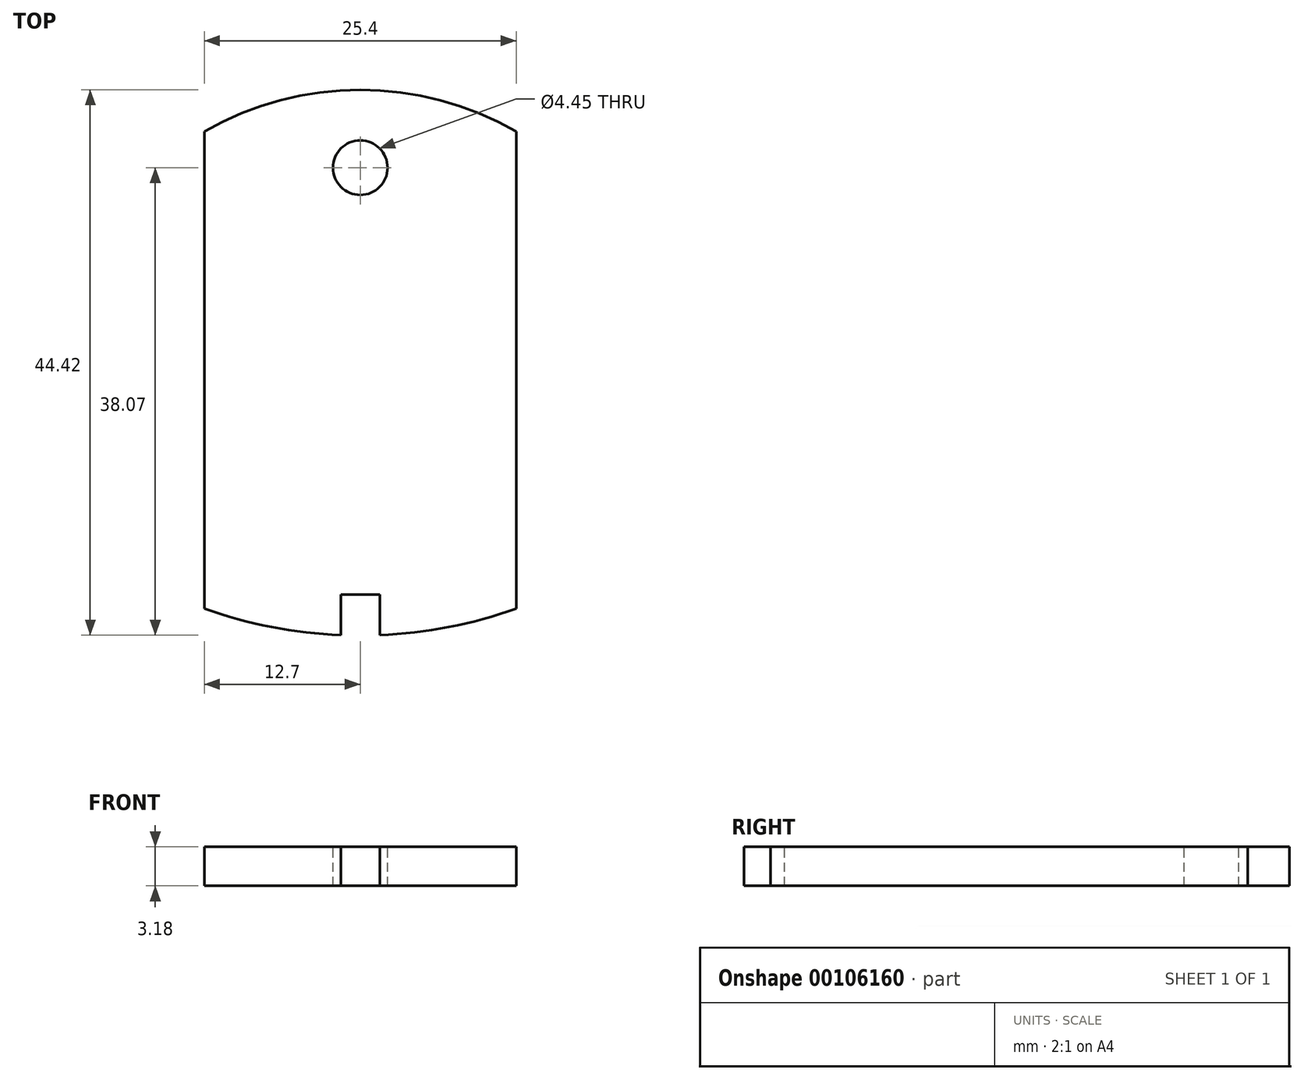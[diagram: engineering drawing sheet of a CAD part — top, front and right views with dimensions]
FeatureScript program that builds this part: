
annotation { "Feature Type Name" : "Feature", "Feature Type Description" : "" }
export const myFeature = defineFeature(function(context is Context, id is Id, definition is map)
    precondition{}
    {
        {
            var Q0;
            Q0=qCreatedBy(makeId("Top.planeOp"),FACE);
            var sketch = newSketch(context, id + "F0", { "sketchPlane" : qUnion([Q0])});
            skLineSegment(sketch, "E0.left", {"start": v(12.7, 47.4) * mm, "end": v(12.7, -47.4) * mm});
            skLineSegment(sketch, "E0.right", {"start": v(-12.7, 47.4) * mm, "end": v(-12.7, -47.4) * mm});
            skPoint(sketch, "E0.middle", {"position": v(0, 0) * mm});
            skLineSegment(sketch, "E1", {"start": v(0, -25.4) * mm, "end": v(0, 25.4) * mm});
            skArc(sketch, "E2", {"start": v(-12.7, -47.4) * mm, "mid": v(0, -50.8) * mm, "end": v(12.7, -47.4) * mm});
            skArc(sketch, "E3.trimOffspring", {"start": v(12.7, 47.4) * mm, "mid": v(0, 50.8) * mm, "end": v(-12.7, 47.4) * mm});
            skPoint(sketch, "E4", {"position": v(0, 50.8) * mm});
            skPoint(sketch, "E5", {"position": v(0, -50.8) * mm});
            skLineSegment(sketch, "E6", {"start": v(-12.7, 0) * mm, "end": v(12.7, 0) * mm});
            skSolve(sketch);
        }
        {
            var Q0;
            Q0=qSketchRegion(id+"F0",true);
            extrude(context, id + "F1", {"entities" : qUnion([Q0]), "depth" : 3.17 * mm});
        }
        {
            var Q0;
            Q0=makeQuery(id+"F1.opExtrude","CAP_FACE",FACE,{"disambiguationData":[OSD([sQuery(id+"F0.wireOp",EDGE,"E0.left"),sQuery(id+"F0.wireOp",EDGE,"E0.right"),sQuery(id+"F0.wireOp",EDGE,"E2"),sQuery(id+"F0.wireOp",EDGE,"E3.trimOffspring")])],"isStart":false});
            var sketch = newSketch(context, id + "F2", { "sketchPlane" : qUnion([Q0])});
            skCircle(sketch, "E7", {"center": v(0, 44.45) * mm, "radius": 2.22 * mm});
            skArc(sketch, "E8", {"start": v(-12.7, 8.53) * mm, "mid": v(-7.22, 7.04) * mm, "end": v(-1.59, 6.38) * mm});
            skLineSegment(sketch, "E9", {"start": v(-12.7, 8.53) * mm, "end": v(-12.7, -47.4) * mm});
            skLineSegment(sketch, "E10", {"start": v(12.7, 8.53) * mm, "end": v(12.7, -47.4) * mm});
            skArc(sketch, "E11", {"start": v(-12.7, -47.4) * mm, "mid": v(0, -50.8) * mm, "end": v(12.7, -47.4) * mm});
            skLineSegment(sketch, "E12.bottom", {"start": v(-1.59, 9.69) * mm, "end": v(1.59, 9.69) * mm});
            skLineSegment(sketch, "E12.left", {"start": v(-1.59, 9.69) * mm, "end": v(-1.59, 6.38) * mm});
            skLineSegment(sketch, "E12.right", {"start": v(1.59, 9.69) * mm, "end": v(1.59, 6.38) * mm});
            skArc(sketch, "E13.trimOffspring", {"start": v(1.59, 6.38) * mm, "mid": v(7.22, 7.04) * mm, "end": v(12.7, 8.53) * mm});
            skLineSegment(sketch, "E14", {"start": v(0, 0) * mm, "end": v(0, 9.69) * mm, "construction": true});
            skSolve(sketch);
        }
        {
            var Q0;
            {var subQ0=sQuery(id+"F2.wireOp",EDGE,"E9");Q0=makeQuery(id+"F2.imprint","IMPRINT",FACE,{"disambiguationData":[TD([[makeQuery(id+"F2.imprint","IMPRINT",EDGE,{"derivedFrom":subQ0}),1.0]])]});}
            var Q1;
            Q1=makeQuery(id+"F2.imprint","IMPRINT",FACE,{"disambiguationData":[TD([[makeQuery(id+"F2.imprint","IMPRINT",EDGE,{"derivedFrom":sQuery(id+"F2.wireOp",EDGE,"DBkJAodz-2GVP-9tsv-b9HE-gXfCkiRO08c6.bottom")}),-1.0]])]});
            var Q2;
            Q2=makeQuery(id+"F2.imprint","IMPRINT",FACE,{"disambiguationData":[TD([[makeQuery(id+"F2.imprint","IMPRINT",EDGE,{"derivedFrom":sQuery(id+"F2.wireOp",EDGE,"E7")}),1.0]])]});
            var Q3;
            {var subQ1=sQuery(id+"F2.wireOp",EDGE,"E12.bottom");Q3=makeQuery(id+"F2.imprint","IMPRINT",FACE,{"disambiguationData":[TD([[makeQuery(id+"F2.imprint","IMPRINT",EDGE,{"derivedFrom":subQ1}),-1.0]])]});}
            extrude(context, id + "F3", {"entities" : qUnion([Q0, Q1, Q2, Q3]), "operationType" : NewBodyOperationType.REMOVE, "oppositeDirection" : true, "depth" : 25.4 * mm});
        }
    });
